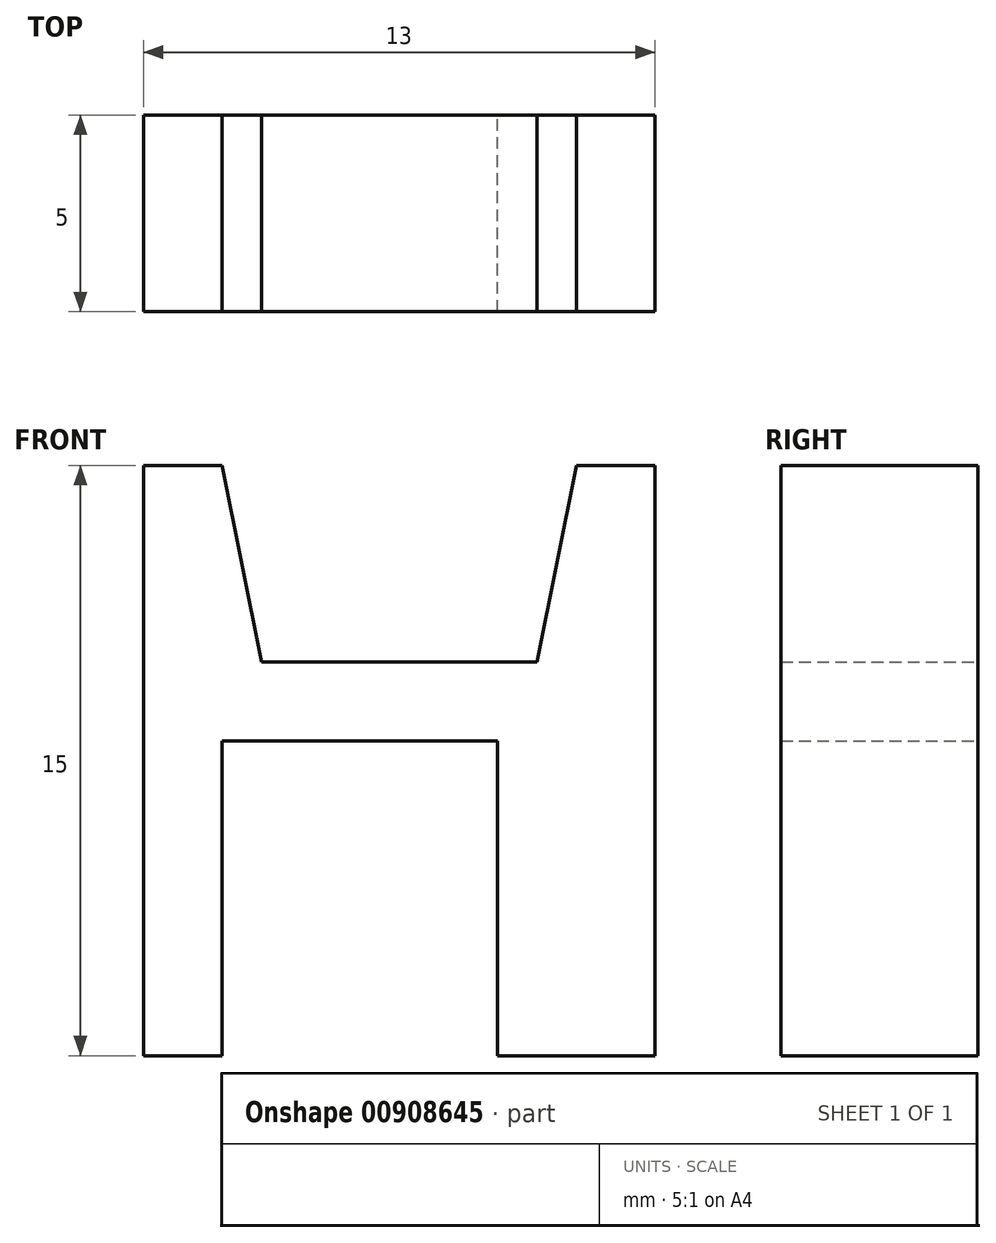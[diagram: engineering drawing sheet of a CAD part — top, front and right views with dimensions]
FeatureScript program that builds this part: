
annotation { "Feature Type Name" : "Feature", "Feature Type Description" : "" }
export const myFeature = defineFeature(function(context is Context, id is Id, definition is map)
    precondition{}
    {
        {
            var Q0;
            Q0=qCreatedBy(makeId("Front.planeOp"),FACE);
            var sketch = newSketch(context, id + "F0", { "sketchPlane" : qUnion([Q0])});
            skLineSegment(sketch, "E0", {"start": v(0, 0) * mm, "end": v(0, 15) * mm});
            skLineSegment(sketch, "E1", {"start": v(0, 15) * mm, "end": v(2, 15) * mm});
            skLineSegment(sketch, "E2", {"start": v(11, 15) * mm, "end": v(13, 15) * mm});
            skLineSegment(sketch, "E3", {"start": v(13, 15) * mm, "end": v(13, 0) * mm});
            skLineSegment(sketch, "E4", {"start": v(13, 0) * mm, "end": v(9, 0) * mm});
            skLineSegment(sketch, "E5", {"start": v(9, 0) * mm, "end": v(9, 8) * mm});
            skLineSegment(sketch, "E6", {"start": v(9, 8) * mm, "end": v(2, 8) * mm});
            skLineSegment(sketch, "E7", {"start": v(2, 8) * mm, "end": v(2, 0) * mm});
            skLineSegment(sketch, "E8", {"start": v(2, 0) * mm, "end": v(0, 0) * mm});
            skLineSegment(sketch, "E9", {"start": v(2, 15) * mm, "end": v(3, 10) * mm});
            skLineSegment(sketch, "E10", {"start": v(3, 10) * mm, "end": v(10, 10) * mm});
            skLineSegment(sketch, "E11", {"start": v(10, 10) * mm, "end": v(11, 15) * mm});
            skSolve(sketch);
        }
        {
            var Q0;
            Q0 = qSketchRegion(id + "F0", true);
            extrude(context, id + "F1", {"entities" : qUnion([Q0]), "depth" : 5 * mm, "offsetDistance" : 25 * mm});
        }
    });
